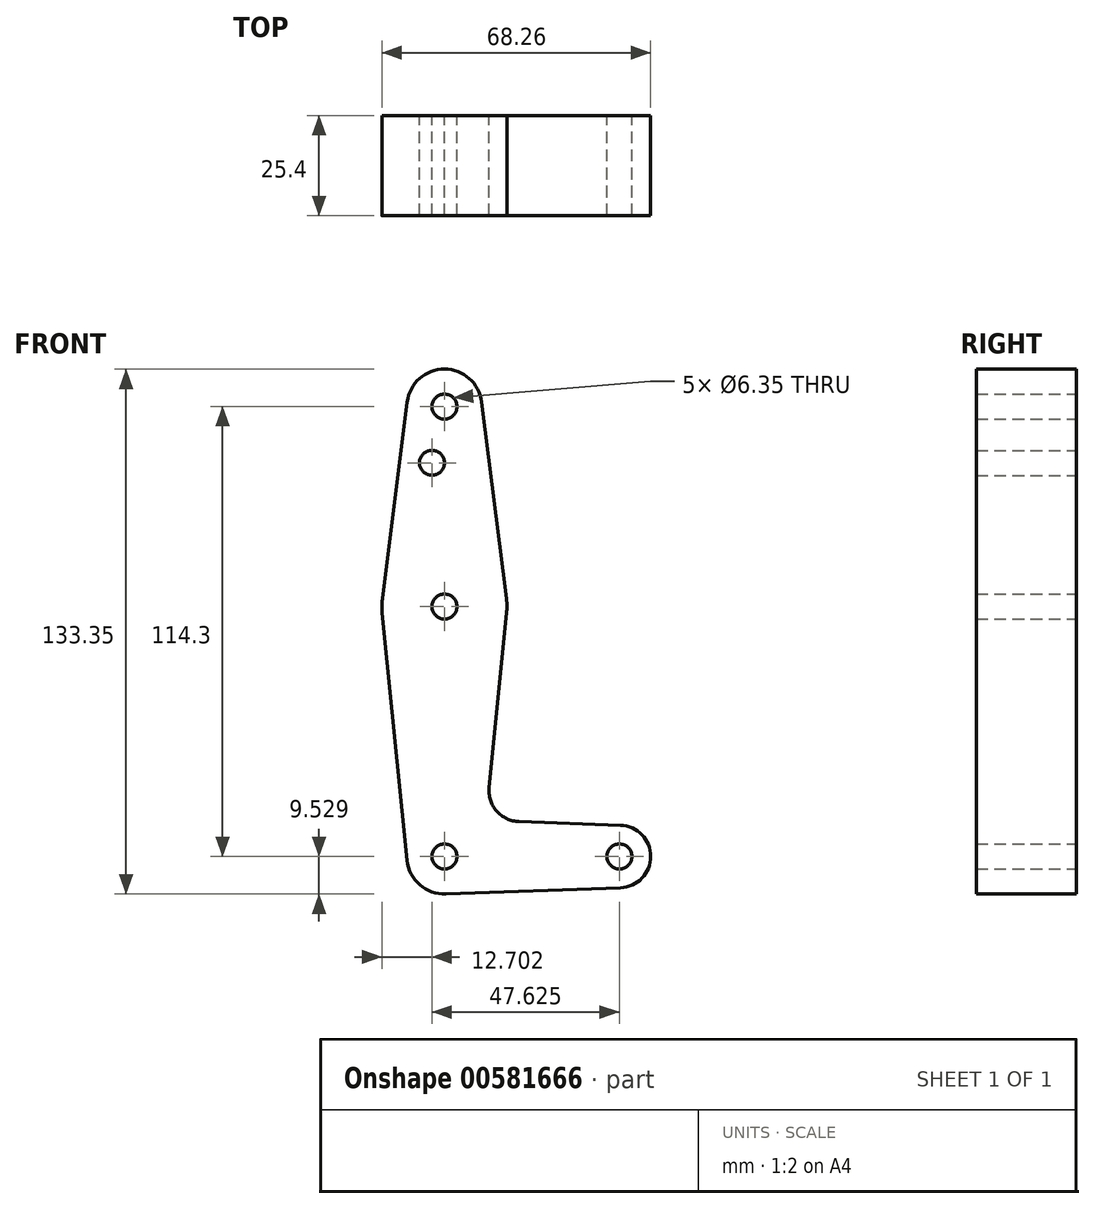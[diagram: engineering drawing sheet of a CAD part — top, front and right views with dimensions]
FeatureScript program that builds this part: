
annotation { "Feature Type Name" : "Feature", "Feature Type Description" : "" }
export const myFeature = defineFeature(function(context is Context, id is Id, definition is map)
    precondition{}
    {
        {
            var Q0;
            Q0=qCreatedBy(makeId("Front.planeOp"),FACE);
            var sketch = newSketch(context, id + "F0", { "sketchPlane" : qUnion([Q0])});
            skCircle(sketch, "E0", {"center": v(-71.22, 67.95) * mm, "radius": 9.53 * mm});
            skCircle(sketch, "E1", {"center": v(-71.22, 17.15) * mm, "radius": 15.88 * mm});
            skCircle(sketch, "E2", {"center": v(-71.22, -46.35) * mm, "radius": 9.53 * mm});
            skCircle(sketch, "E3", {"center": v(-26.77, -46.35) * mm, "radius": 7.94 * mm});
            skLineSegment(sketch, "E4", {"start": v(-71.22, 67.95) * mm, "end": v(-71.22, 17.15) * mm, "construction": true});
            skLineSegment(sketch, "E5", {"start": v(-71.22, -46.35) * mm, "end": v(-26.77, -46.35) * mm, "construction": true});
            skLineSegment(sketch, "E6", {"start": v(-71.22, 17.15) * mm, "end": v(-71.22, -46.35) * mm, "construction": true});
            skLineSegment(sketch, "E7", {"start": v(-80.67, 69.14) * mm, "end": v(-86.97, 19.13) * mm});
            skLineSegment(sketch, "E8", {"start": v(-61.77, 69.14) * mm, "end": v(-55.47, 19.13) * mm});
            skLineSegment(sketch, "E9", {"start": v(-87.02, 15.56) * mm, "end": v(-80.7, -47.3) * mm});
            skLineSegment(sketch, "E10", {"start": v(-55.43, 15.56) * mm, "end": v(-59.88, -28.76) * mm});
            skLineSegment(sketch, "E11", {"start": v(-52.26, -37.5) * mm, "end": v(-26.49, -38.42) * mm});
            skLineSegment(sketch, "E12", {"start": v(-70.88, -55.87) * mm, "end": v(-26.49, -54.28) * mm});
            skArc(sketch, "E13.filletArc", {"start": v(-59.88, -28.76) * mm, "mid": v(-57.96, -34.78) * mm, "end": v(-52.26, -37.5) * mm});
            skCircle(sketch, "E14", {"center": v(-71.22, 67.95) * mm, "radius": 3.18 * mm});
            skCircle(sketch, "E15", {"center": v(-71.22, 17.15) * mm, "radius": 3.18 * mm});
            skCircle(sketch, "E16", {"center": v(-71.22, -46.35) * mm, "radius": 3.18 * mm});
            skCircle(sketch, "E17", {"center": v(-26.77, -46.35) * mm, "radius": 3.18 * mm});
            skCircle(sketch, "E18", {"center": v(-74.4, 53.67) * mm, "radius": 3.18 * mm});
            skSolve(sketch);
        }
        {
            var Q0;
            Q0=makeQuery(id+"F0.imprint","IMPRINT",FACE,{"disambiguationData":[TD([[makeQuery(id+"F0.imprint","IMPRINT",EDGE,{"derivedFrom":sQuery(id+"F0.wireOp",EDGE,"E14")}),-1.0]])]});
            var Q1;
            {var subQ0=sQuery(id+"F0.wireOp",EDGE,"E7");Q1=makeQuery(id+"F0.imprint","IMPRINT",FACE,{"disambiguationData":[TD([[makeQuery(id+"F0.imprint","IMPRINT",EDGE,{"derivedFrom":subQ0}),1.0]])]});}
            var Q2;
            Q2=makeQuery(id+"F0.imprint","IMPRINT",FACE,{"disambiguationData":[TD([[makeQuery(id+"F0.imprint","IMPRINT",EDGE,{"derivedFrom":sQuery(id+"F0.wireOp",EDGE,"E15")}),-1.0]])]});
            var Q3;
            {var subQ3=sQuery(id+"F0.wireOp",EDGE,"E9");Q3=makeQuery(id+"F0.imprint","IMPRINT",FACE,{"disambiguationData":[TD([[makeQuery(id+"F0.imprint","IMPRINT",EDGE,{"derivedFrom":subQ3}),1.0]])]});}
            var Q4;
            Q4=makeQuery(id+"F0.imprint","IMPRINT",FACE,{"disambiguationData":[TD([[makeQuery(id+"F0.imprint","IMPRINT",EDGE,{"derivedFrom":sQuery(id+"F0.wireOp",EDGE,"E16")}),-1.0]])]});
            var Q5;
            Q5=makeQuery(id+"F0.imprint","IMPRINT",FACE,{"disambiguationData":[TD([[makeQuery(id+"F0.imprint","IMPRINT",EDGE,{"derivedFrom":sQuery(id+"F0.wireOp",EDGE,"E17")}),-1.0]])]});
            extrude(context, id + "F1", {"entities" : qUnion([Q0, Q1, Q2, Q3, Q4, Q5]), "depth" : 25.4 * mm, "offsetDistance" : 25.4 * mm});
        }
    });
